# Revit family: Турникет трипод PERCo_TTR-11А
name_source: partatom
category: Оборудование
units: mm (PartAtom-declared; Revit-internal decimal feet)

## family parameters
Всегда вертикально = Нет
Классификация = Нет
На основе рабочей плоскости = Нет
Общий = Нет
При загрузке вырезать с полостями = Нет
Размер круглого соединителя = Использовать диаметр
Тип детали = Нормальный
Точка расчета площади = Нет

## types (1)
- TTR-11A
    ADSK_URL страницы изделия = https://www.perco.ru
    ADSK_Единица измерения = шт.
    ADSK_Завод-изготовитель = PERCo
    ADSK_Количество = 1
    ADSK_Масса_Текст = не более 75 кг
    ADSK_Материал наименование = Внешний корпус турникета выполнен из высококачественной нержавеющей стали, передняя панель – из металлического листа, покрытого порошковой краской, верхняя поверхность колпака – из слоистого пластика со вставкой из поликарбоната. Планки из нержавеющей стали.
    ADSK_Наименование = Турникет моторизованный PERCo-TTR-11А с автоматическими планками «Антипаника»
    ADSK_Наименование краткое = Турникет TTR-11А
    ADSK_Напряжение = 24 В
    ADSK_Номинальная мощность = 150 Вт
    ADSK_Ток = 6 А
    Встраивание считывателей внутрь = Да
    Габаритные размеры (длина×ширина×высота) = 800×760×1055 мм
    Габаритные размеры контроллера для встраивания в нишу = Не предусмотрено
    Габаритные размеры считывателя для встраивания в ниши = не более 145×70×28 мм
    Длина планки = 537 мм
    Корпус = Нержавейка
    Корпус_покрытие = панель
    Материал планок = Нержавейка
    Основание планки = Черный
    Подключение к электросети = 220 В
    Покрытие турникета = Черный
    Пропускная способность = 30 чел./мин
    Степень защиты оболочки = IP42
    Температура использования = от -40°С до +50°С
    Цвет = нержавейка
    Ширина зоны прохода = 500 мм.
